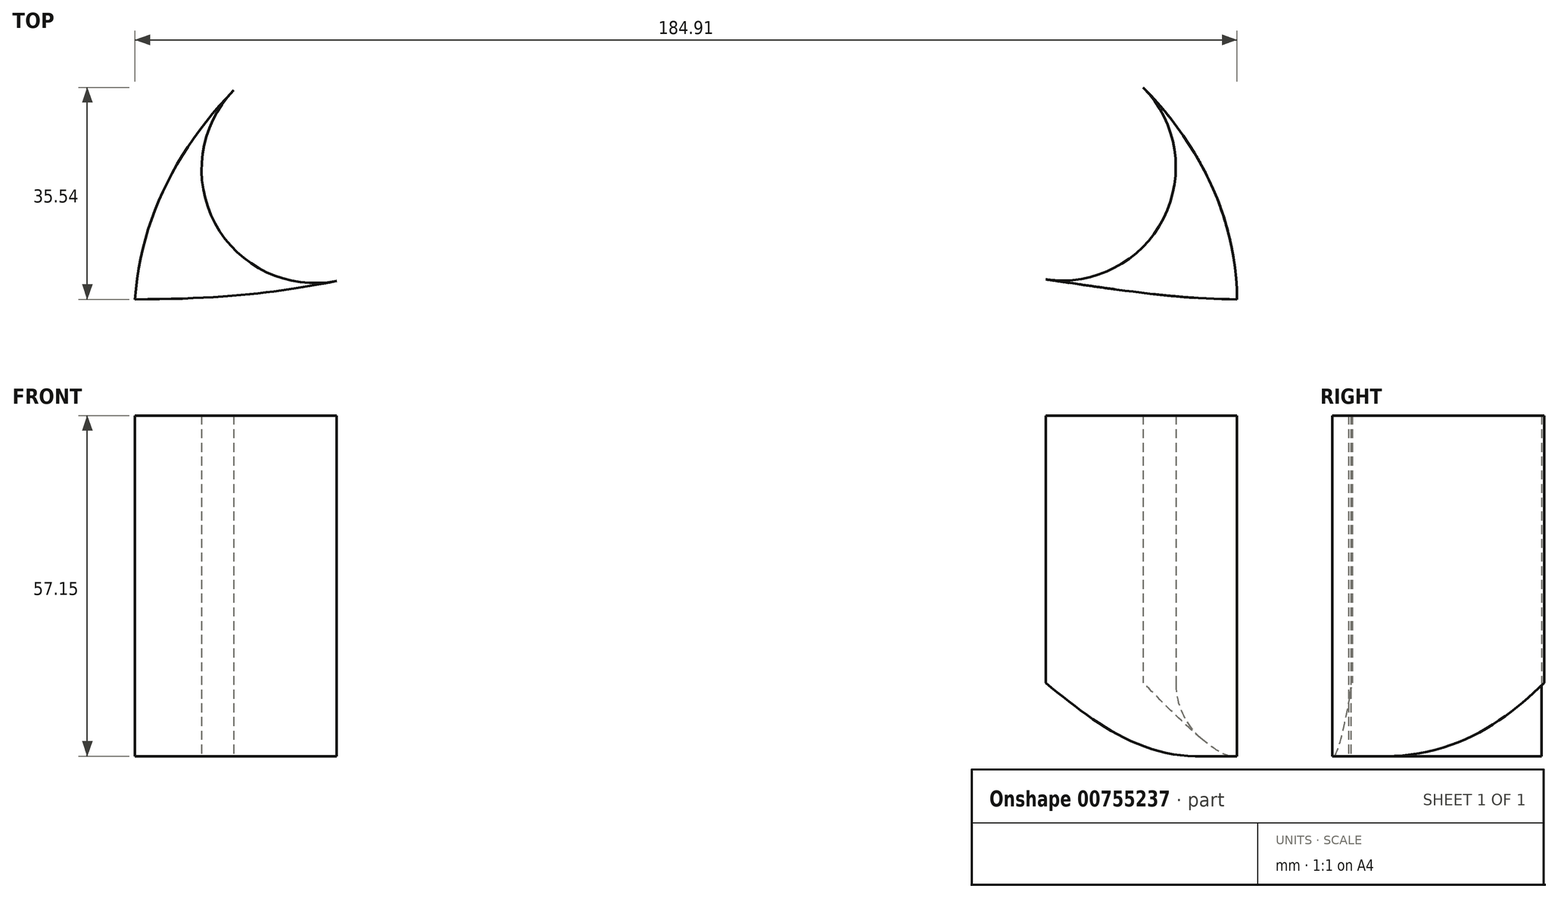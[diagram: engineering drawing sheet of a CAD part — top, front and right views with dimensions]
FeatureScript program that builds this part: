
annotation { "Feature Type Name" : "Feature", "Feature Type Description" : "" }
export const myFeature = defineFeature(function(context is Context, id is Id, definition is map)
    precondition{}
    {
        {
            var Q0;
            Q0=qCreatedBy(makeId("Top.planeOp"),FACE);
            var sketch = newSketch(context, id + "F0", { "sketchPlane" : qUnion([Q0])});
            skFitSpline(sketch, "E0", {"points": [v(-89.8, 0) * mm, v(0, 63.81) * mm, v(95.11, 0) * mm], "startDerivative": vector(15.21, 223.85) * mm, "endDerivative": vector(3.62, -237.04) * mm});
            skFitSpline(sketch, "E1", {"points": [v(-89.8, 0) * mm, v(-40.96, 5.72) * mm, v(39.74, 6.3) * mm, v(95.11, 0) * mm], "startDerivative": vector(259.11, 0) * mm, "endDerivative": vector(149.53, 0) * mm});
            skArc(sketch, "E2.filletArc", {"start": v(-73.24, 35.06) * mm, "mid": v(-76.36, 12.74) * mm, "end": v(-56, 3.07) * mm});
            skArc(sketch, "E3.filletArc", {"start": v(63.02, 3.34) * mm, "mid": v(82.77, 13.57) * mm, "end": v(79.37, 35.54) * mm});
            skSolve(sketch);
        }
        {
            var Q0;
            Q0=makeQuery(id+"F0.imprint","IMPRINT",FACE,{"disambiguationData":[TD([[makeQuery(id+"F0.imprint","IMPRINT",EDGE,{"derivedFrom":sQuery(id+"F0.wireOp",EDGE,"E0")}),-1.0]])]});
            extrude(context, id + "F1", {"entities" : qUnion([Q0]), "depth" : 57.15 * mm, "offsetDistance" : 25.4 * mm});
        }
        {
            var Q0;
            Q0=makeQuery(id+"F1.opExtrude","CAP_EDGE",EDGE,{"disambiguationData":[OSD([sQuery(id+"F0.wireOp",EDGE,"E3.filletArc")])],"isStart":true});
            fillet(context, id + "F2", {"entities" : qUnion([Q0]), "radius" : 12.26 * mm, "tangentPropagation" : true, "allowEdgeOverflow" : false});
        }
    });
